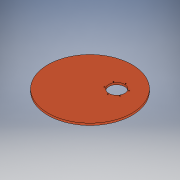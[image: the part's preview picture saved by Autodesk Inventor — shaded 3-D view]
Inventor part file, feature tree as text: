
AUTODESK INVENTOR PART (.ipt)
format: ipt  version: 2018 (Build 220112000, 112)  size: 120,320 bytes
history: native  units: in
note: dims shown in document units (in); Inventor stores cm internally (conversion verified against a paired STEP export)
features: sketch x3, extrude x2, hole x1
ambient origin geometry x8: Origin, YZ Plane, XZ Plane, XY Plane, X Axis, Y Axis, Z Axis, Center Point
bodies: Solid1 (feature_tree)
feature tree (6):
  extrude  "Extrusion1"  Depth=0.375in TaperAngle=0.0deg
  hole  "Hole1"  [1 undecoded]
  extrude  "Extrusion2"  TaperAngle=30.0deg  [1 undecoded]
  sketch  "Sketch1"  dims[d0=16.0in d1=0.375in d2=0.0in]
  sketch  "Sketch2"  dims[d3=3.6in d4=45.0deg]
  sketch  "Sketch3"  dims[d5=1.7in d6=30.0deg d7=2.3622in d9=360.0deg d11=0.163in d12=0.394in d13=0.375in d14=0.25in d15=0.5635in d16=0.559in d17=0.8108in d18=3.6in d19=45.0deg d20=3.0in d21=0.375in d22=0.0in]
note: 2 required parameter values undecoded (feature->parameter linkage not recoverable at this tier; creation-order binding heuristic only, values carry confidence <= 0.55)
